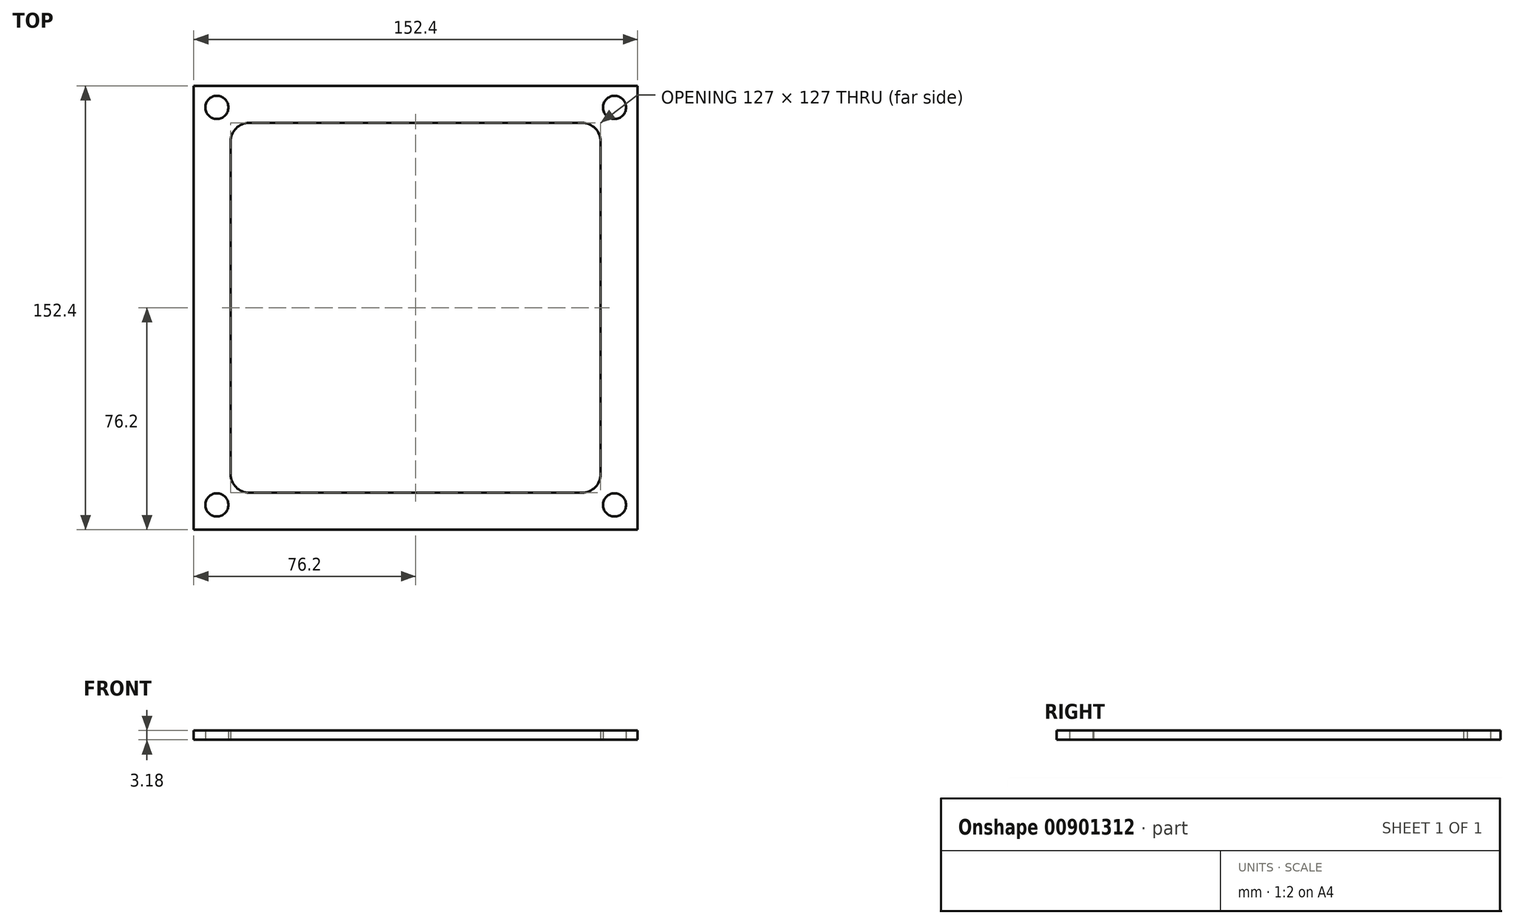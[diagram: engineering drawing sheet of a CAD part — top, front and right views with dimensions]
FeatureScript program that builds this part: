
annotation { "Feature Type Name" : "Feature", "Feature Type Description" : "" }
export const myFeature = defineFeature(function(context is Context, id is Id, definition is map)
    precondition{}
    {
        {
            var Q0;
            Q0=qCreatedBy(makeId("Top.planeOp"),FACE);
            var sketch = newSketch(context, id + "F0", { "sketchPlane" : qUnion([Q0])});
            skLineSegment(sketch, "E0.bottom", {"start": v(0, 0) * mm, "end": v(152.4, 0) * mm});
            skLineSegment(sketch, "E0.top", {"start": v(0, 152.4) * mm, "end": v(152.4, 152.4) * mm});
            skLineSegment(sketch, "E0.left", {"start": v(0, 0) * mm, "end": v(0, 152.4) * mm});
            skLineSegment(sketch, "E0.right", {"start": v(152.4, 0) * mm, "end": v(152.4, 152.4) * mm});
            skLineSegment(sketch, "E1.bottom", {"start": v(19.05, 12.7) * mm, "end": v(133.35, 12.7) * mm});
            skLineSegment(sketch, "E1.top", {"start": v(19.05, 139.7) * mm, "end": v(133.35, 139.7) * mm});
            skLineSegment(sketch, "E1.left", {"start": v(12.7, 19.05) * mm, "end": v(12.7, 133.35) * mm});
            skLineSegment(sketch, "E1.right", {"start": v(139.7, 19.05) * mm, "end": v(139.7, 133.35) * mm});
            skCircle(sketch, "E2", {"center": v(7.94, 8.5) * mm, "radius": 3.97 * mm});
            skPoint(sketch, "E3.visualSharp", {"position": v(12.7, 12.7) * mm});
            skArc(sketch, "E3.filletArc", {"start": v(12.7, 19.05) * mm, "mid": v(14.56, 14.56) * mm, "end": v(19.05, 12.7) * mm});
            skPoint(sketch, "E4.visualSharp", {"position": v(139.7, 12.7) * mm});
            skArc(sketch, "E4.filletArc", {"start": v(133.35, 12.7) * mm, "mid": v(137.84, 14.56) * mm, "end": v(139.7, 19.05) * mm});
            skPoint(sketch, "E5.visualSharp", {"position": v(139.7, 139.7) * mm});
            skArc(sketch, "E5.filletArc", {"start": v(139.7, 133.35) * mm, "mid": v(137.84, 137.84) * mm, "end": v(133.35, 139.7) * mm});
            skCircle(sketch, "E6.0.1.0", {"center": v(7.94, 145.02) * mm, "radius": 3.97 * mm});
            skCircle(sketch, "E6.1.0.0", {"center": v(144.46, 8.5) * mm, "radius": 3.97 * mm});
            skCircle(sketch, "E6.1.1.0", {"center": v(144.46, 145.02) * mm, "radius": 3.97 * mm});
            skLineSegment(sketch, "E6.direction1", {"start": v(7.94, 8.5) * mm, "end": v(144.46, 8.5) * mm, "construction": true});
            skLineSegment(sketch, "E6.direction2", {"start": v(7.94, 8.5) * mm, "end": v(7.94, 145.02) * mm, "construction": true});
            skPoint(sketch, "E7.visualSharp", {"position": v(12.7, 139.7) * mm});
            skArc(sketch, "E7.filletArc", {"start": v(19.05, 139.7) * mm, "mid": v(14.56, 137.84) * mm, "end": v(12.7, 133.35) * mm});
            skSolve(sketch);
        }
        {
            var Q0;
            Q0=makeQuery(id+"F0.imprint","IMPRINT",FACE,{"disambiguationData":[TD([[makeQuery(id+"F0.imprint","IMPRINT",EDGE,{"derivedFrom":sQuery(id+"F0.wireOp",EDGE,"E0.bottom")}),1.0]])]});
            extrude(context, id + "F1", {"entities" : qUnion([Q0]), "depth" : 3.17 * mm, "offsetDistance" : 25.4 * mm});
        }
    });
